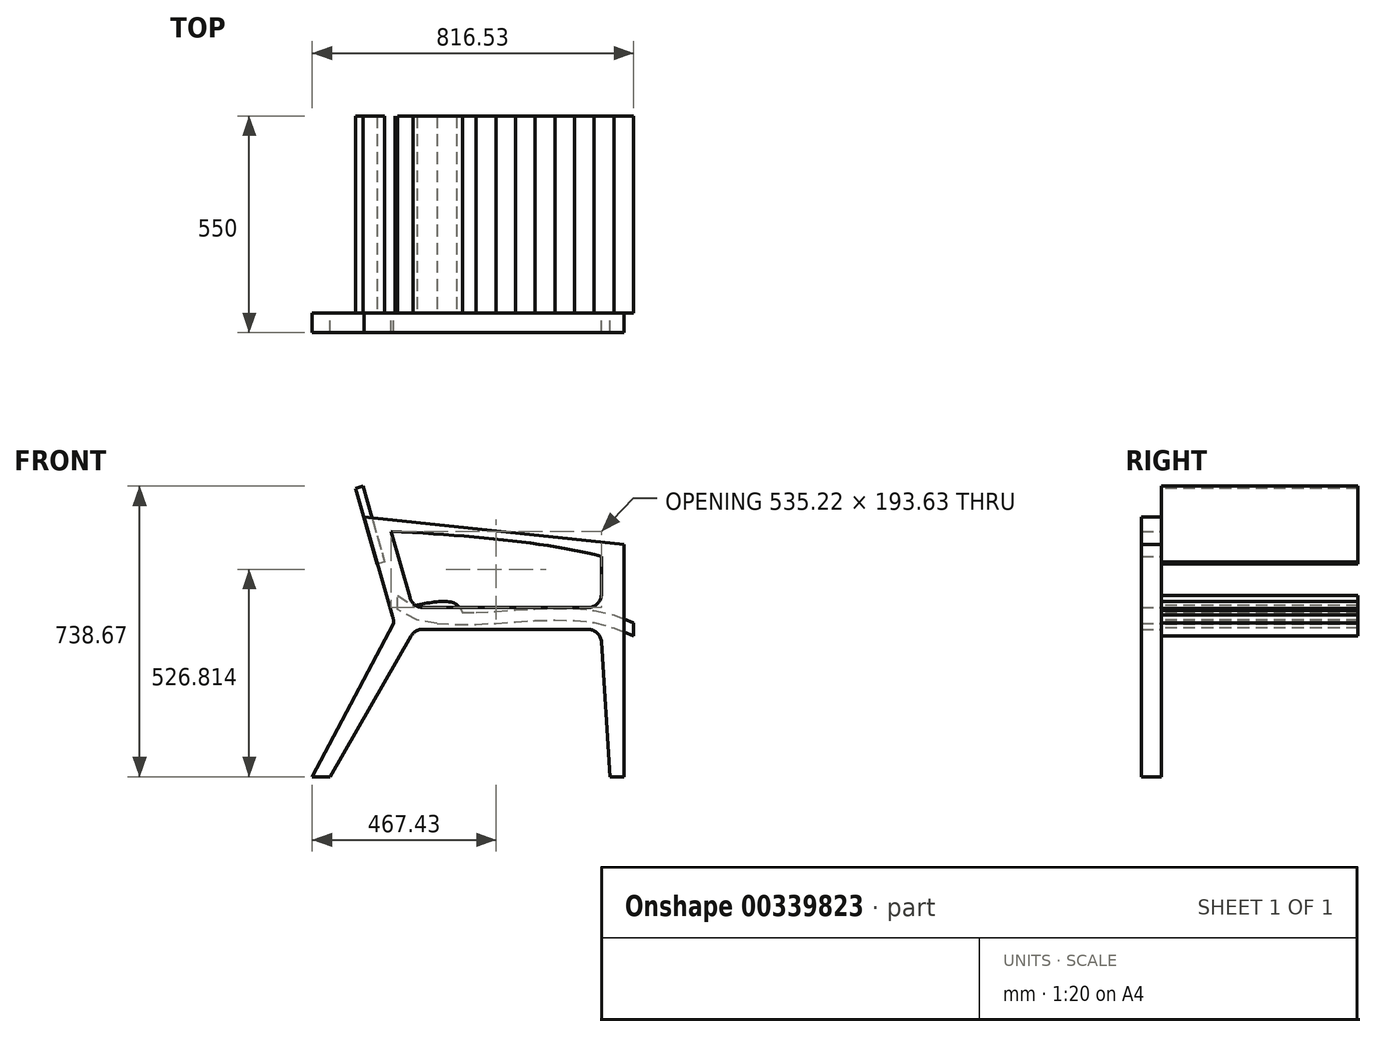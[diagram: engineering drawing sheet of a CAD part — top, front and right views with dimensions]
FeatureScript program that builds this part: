
annotation { "Feature Type Name" : "Feature", "Feature Type Description" : "" }
export const myFeature = defineFeature(function(context is Context, id is Id, definition is map)
    precondition{}
    {
        {
            var Q0;
            Q0=qCreatedBy(makeId("Front.planeOp"),FACE);
            var sketch = newSketch(context, id + "F0", { "sketchPlane" : qUnion([Q0])});
            skLineSegment(sketch, "E0", {"start": v(-160.06, 0) * mm, "end": v(258.26, 0) * mm});
            skLineSegment(sketch, "E1.0", {"start": v(-160.06, -55) * mm, "end": v(258.26, -55) * mm});
            skLineSegment(sketch, "E2.0", {"start": v(349.94, 160) * mm, "end": v(349.94, -430) * mm});
            skLineSegment(sketch, "E3", {"start": v(-193.7, 25.35) * mm, "end": v(-241.96, 193.63) * mm});
            skLineSegment(sketch, "E4", {"start": v(-190.37, -72.5) * mm, "end": v(-396.78, -430) * mm});
            skLineSegment(sketch, "E5.0", {"start": v(349.73, -430) * mm, "end": v(348.96, -430) * mm});
            skLineSegment(sketch, "E6", {"start": v(349.73, -430) * mm, "end": v(349.94, -430) * mm});
            skLineSegment(sketch, "E7", {"start": v(-396.78, -430) * mm, "end": v(-441.78, -430) * mm});
            skLineSegment(sketch, "E8.0", {"start": v(-237.12, -22.78) * mm, "end": v(-309.6, 230) * mm});
            skArc(sketch, "E9.filletArc", {"start": v(-160.06, -55) * mm, "mid": v(-177.56, -59.69) * mm, "end": v(-190.37, -72.5) * mm});
            skArc(sketch, "E10.filletArc", {"start": v(-235.33, -40.37) * mm, "mid": v(-235.44, -31.5) * mm, "end": v(-237.12, -22.78) * mm});
            skArc(sketch, "E11.filletArc", {"start": v(-193.7, 25.35) * mm, "mid": v(-181.13, 7.05) * mm, "end": v(-160.06, 0) * mm});
            skLineSegment(sketch, "E12", {"start": v(-235.33, -40.37) * mm, "end": v(-441.78, -430) * mm});
            skLineSegment(sketch, "E13", {"start": v(293.26, 35) * mm, "end": v(293.26, 130) * mm});
            skFitSpline(sketch, "E14", {"points": [v(-241.96, 193.63) * mm, v(293.26, 130) * mm, v(482.35, 46.07) * mm], "startDerivative": vector(1025.62, -54.46) * mm, "endDerivative": vector(365.11, -259.67) * mm});
            skLineSegment(sketch, "E15", {"start": v(349.94, 160) * mm, "end": v(293.26, 130) * mm});
            skLineSegment(sketch, "E16", {"start": v(-309.6, 230) * mm, "end": v(349.94, 160) * mm});
            skLineSegment(sketch, "E17", {"start": v(-241.96, 193.63) * mm, "end": v(-309.6, 230) * mm});
            skLineSegment(sketch, "E18", {"start": v(349.94, -430) * mm, "end": v(314.94, -430) * mm});
            skLineSegment(sketch, "E19", {"start": v(293.2, -87.78) * mm, "end": v(314.94, -430) * mm});
            skArc(sketch, "E20", {"start": v(-160.06, 0) * mm, "mid": v(-166.74, -27.5) * mm, "end": v(-160.06, -55) * mm});
            skArc(sketch, "E21.filletArc", {"start": v(258.26, 0) * mm, "mid": v(283, 10.25) * mm, "end": v(293.26, 35) * mm});
            skArc(sketch, "E22.filletArc", {"start": v(293.2, -87.78) * mm, "mid": v(282.21, -64.48) * mm, "end": v(258.26, -55) * mm});
            skArc(sketch, "E23", {"start": v(258.26, -55) * mm, "mid": v(264.93, -27.5) * mm, "end": v(258.26, 0) * mm});
            skLineSegment(sketch, "E24", {"start": v(-396.78, -430) * mm, "end": v(314.94, -430) * mm, "construction": true});
            skLineSegment(sketch, "E25", {"start": v(-235.33, -31.5) * mm, "end": v(-358.73, -31.5) * mm});
            skPoint(sketch, "E25.startSnap0", {"position": v(-235.44, -31.5) * mm});
            skSolve(sketch);
        }
        {
            var Q0;
            Q0=qCreatedBy(makeId("Front.planeOp"),FACE);
            var sketch = newSketch(context, id + "F1", { "sketchPlane" : qUnion([Q0])});
            skLineSegment(sketch, "E26", {"start": v(-332.25, 303.17) * mm, "end": v(-277.26, 110.88) * mm});
            skLineSegment(sketch, "E27", {"start": v(-313.02, 308.67) * mm, "end": v(-258.03, 116.38) * mm});
            skPoint(sketch, "E28.startDerivative.orphan", {"position": v(70.06, -25.15) * mm});
            skLineSegment(sketch, "E29.0", {"start": v(324.75, -19.2) * mm, "end": v(324.75, -51.55) * mm});
            skLineSegment(sketch, "E30.0", {"start": v(274.75, -7.22) * mm, "end": v(274.75, -38.07) * mm});
            skLineSegment(sketch, "E31.0", {"start": v(224.75, -2.52) * mm, "end": v(224.75, -32.65) * mm});
            skLineSegment(sketch, "E32.0", {"start": v(174.75, -1.66) * mm, "end": v(174.75, -31.67) * mm});
            skLineSegment(sketch, "E33.0", {"start": v(124.75, -3.2) * mm, "end": v(124.75, -33.25) * mm});
            skLineSegment(sketch, "E34.0", {"start": v(24.75, -10.03) * mm, "end": v(24.75, -40.06) * mm});
            skLineSegment(sketch, "E35.0", {"start": v(-25.25, -12.37) * mm, "end": v(-25.25, -42.37) * mm});
            skLineSegment(sketch, "E36.0", {"start": v(-75.25, -12.7) * mm, "end": v(-75.25, -42.7) * mm});
            skLineSegment(sketch, "E37.0", {"start": v(-175.25, -1.37) * mm, "end": v(-175.25, -31.8) * mm});
            skFitSpline(sketch, "E38", {"points": [v(-226.6, 30.57) * mm, v(-225.69, 3.87) * mm, v(-86.7, 13.22) * mm, v(-52.2, -57) * mm], "startDerivative": vector(-26.4, -144.35) * mm, "endDerivative": vector(27.59, -264.6) * mm});
            skLineSegment(sketch, "E39.0", {"start": v(-231.59, -1.43) * mm, "end": v(-231.59, -1.44) * mm});
            skLineSegment(sketch, "E40", {"start": v(-175.25, -1.37) * mm, "end": v(-125.25, -9.86) * mm});
            skLineSegment(sketch, "E41", {"start": v(-125.25, -9.86) * mm, "end": v(-75.25, -12.7) * mm});
            skLineSegment(sketch, "E42", {"start": v(-75.25, -12.7) * mm, "end": v(-25.25, -12.37) * mm});
            skLineSegment(sketch, "E43", {"start": v(-25.25, -12.37) * mm, "end": v(24.75, -10.03) * mm});
            skLineSegment(sketch, "E44", {"start": v(24.75, -10.03) * mm, "end": v(74.75, -6.35) * mm});
            skLineSegment(sketch, "E45", {"start": v(74.75, -6.35) * mm, "end": v(124.75, -3.2) * mm});
            skLineSegment(sketch, "E46", {"start": v(124.75, -3.2) * mm, "end": v(174.75, -1.66) * mm});
            skLineSegment(sketch, "E47", {"start": v(174.75, -1.66) * mm, "end": v(224.75, -2.52) * mm});
            skLineSegment(sketch, "E48", {"start": v(224.75, -2.52) * mm, "end": v(274.75, -7.22) * mm});
            skLineSegment(sketch, "E49", {"start": v(274.75, -7.22) * mm, "end": v(324.75, -19.2) * mm});
            skLineSegment(sketch, "E50", {"start": v(324.75, -19.2) * mm, "end": v(374.75, -39.4) * mm});
            skLineSegment(sketch, "E51.0", {"start": v(324.75, -51.55) * mm, "end": v(374.75, -71.76) * mm});
            skLineSegment(sketch, "E51.6", {"start": v(-231.6, -1.43) * mm, "end": v(-231.59, -1.43) * mm});
            skLineSegment(sketch, "E51.7", {"start": v(-75.25, -42.7) * mm, "end": v(-25.25, -42.37) * mm});
            skLineSegment(sketch, "E52", {"start": v(-231.6, -1.43) * mm, "end": v(-231.59, -1.44) * mm});
            skLineSegment(sketch, "E53.trimOffspring", {"start": v(-175.25, -52.88) * mm, "end": v(-175.25, -54.07) * mm});
            skLineSegment(sketch, "E54.trimOffspring", {"start": v(174.75, -52.88) * mm, "end": v(174.75, -54.07) * mm});
            skLineSegment(sketch, "E55.trimOffspring", {"start": v(124.75, -52.88) * mm, "end": v(124.75, -54.07) * mm});
            skLineSegment(sketch, "E56.trimOffspring", {"start": v(74.75, -52.88) * mm, "end": v(74.75, -54.07) * mm});
            skLineSegment(sketch, "E57", {"start": v(-125.25, -9.86) * mm, "end": v(-125.25, -39.9) * mm});
            skLineSegment(sketch, "E58", {"start": v(74.75, -6.35) * mm, "end": v(74.75, -36.28) * mm});
            skLineSegment(sketch, "E59", {"start": v(-125.25, -39.9) * mm, "end": v(-175.25, -31.8) * mm});
            skLineSegment(sketch, "E60", {"start": v(-125.25, -39.9) * mm, "end": v(-75.25, -42.7) * mm});
            skPoint(sketch, "E61.orphan", {"position": v(76.8, -36.28) * mm});
            skLineSegment(sketch, "E62", {"start": v(-25.25, -42.37) * mm, "end": v(24.75, -40.06) * mm});
            skLineSegment(sketch, "E63", {"start": v(24.75, -40.06) * mm, "end": v(74.75, -36.28) * mm});
            skLineSegment(sketch, "E64", {"start": v(74.75, -36.28) * mm, "end": v(124.75, -33.25) * mm});
            skLineSegment(sketch, "E65", {"start": v(124.75, -33.25) * mm, "end": v(174.75, -31.67) * mm});
            skLineSegment(sketch, "E66", {"start": v(174.75, -31.67) * mm, "end": v(224.75, -32.65) * mm});
            skLineSegment(sketch, "E67", {"start": v(224.75, -32.65) * mm, "end": v(274.75, -38.07) * mm});
            skLineSegment(sketch, "E68", {"start": v(274.75, -38.07) * mm, "end": v(324.75, -51.55) * mm});
            skLineSegment(sketch, "E69", {"start": v(-225.25, 30.57) * mm, "end": v(-175.25, -1.37) * mm});
            skLineSegment(sketch, "E70", {"start": v(-175.25, -31.8) * mm, "end": v(-225.25, -4.67) * mm});
            skLineSegment(sketch, "E71", {"start": v(-225.25, -4.67) * mm, "end": v(-225.25, 30.57) * mm});
            skLineSegment(sketch, "E72", {"start": v(374.75, -39.4) * mm, "end": v(374.75, -71.76) * mm});
            skLineSegment(sketch, "E73", {"start": v(-258.03, 116.38) * mm, "end": v(-277.26, 110.88) * mm});
            skLineSegment(sketch, "E74.0", {"start": v(-271.78, 164.45) * mm, "end": v(-291, 158.96) * mm});
            skLineSegment(sketch, "E75.0", {"start": v(-285.53, 212.53) * mm, "end": v(-304.76, 207.03) * mm});
            skLineSegment(sketch, "E76.0", {"start": v(-299.28, 260.6) * mm, "end": v(-318.5, 255.1) * mm});
            skLineSegment(sketch, "E77.0", {"start": v(-313.02, 308.67) * mm, "end": v(-332.25, 303.17) * mm});
            skSolve(sketch);
        }
        {
            var Q0;
            Q0 = qSketchRegion(id + "F1", true);
            extrude(context, id + "F2", {"entities" : qUnion([Q0]), "oppositeDirection" : true, "offsetDistance" : 25 * mm, "depth" : 500 * mm});
        }
        {
            var Q0;
            Q0 = qSketchRegion(id + "F0", true);
            extrude(context, id + "F3", {"entities" : qUnion([Q0]), "offsetDistance" : 25 * mm, "depth" : 50 * mm});
        }
    });
